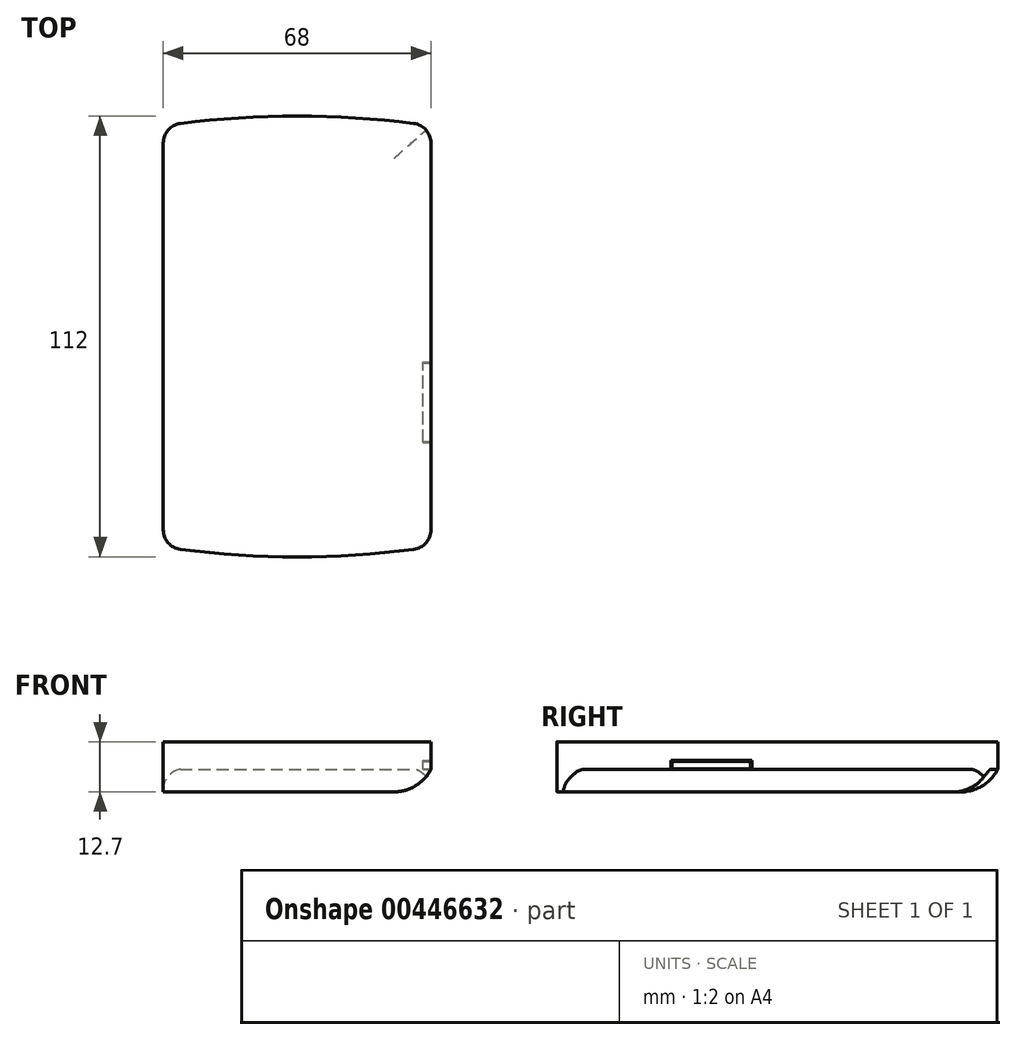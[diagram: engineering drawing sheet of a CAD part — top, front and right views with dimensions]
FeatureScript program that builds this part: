
annotation { "Feature Type Name" : "Feature", "Feature Type Description" : "" }
export const myFeature = defineFeature(function(context is Context, id is Id, definition is map)
    precondition{}
    {
        {
            var Q0;
            Q0=qCreatedBy(makeId("Top.planeOp"),FACE);
            var sketch = newSketch(context, id + "F0", { "sketchPlane" : qUnion([Q0])});
            skLineSegment(sketch, "E0.left", {"start": v(-34, 49.14) * mm, "end": v(-34, -49.14) * mm});
            skLineSegment(sketch, "E0.right", {"start": v(34, 49.14) * mm, "end": v(34, -49.14) * mm});
            skLineSegment(sketch, "E1", {"start": v(-34, 0) * mm, "end": v(34, 0) * mm, "construction": true});
            skArc(sketch, "E2", {"start": v(29.64, 54.1) * mm, "mid": v(0, 56) * mm, "end": v(-29.64, 54.1) * mm});
            skArc(sketch, "E3", {"start": v(-29.64, -54.1) * mm, "mid": v(0, -56) * mm, "end": v(29.64, -54.1) * mm});
            skLineSegment(sketch, "E4", {"start": v(0, 56) * mm, "end": v(0, -56) * mm, "construction": true});
            skPoint(sketch, "E5.visualSharp", {"position": v(-34, 53.5) * mm});
            skArc(sketch, "E5.filletArc", {"start": v(-29.64, 54.1) * mm, "mid": v(-32.75, 52.45) * mm, "end": v(-34, 49.14) * mm});
            skPoint(sketch, "E6.visualSharp", {"position": v(34, 53.5) * mm});
            skArc(sketch, "E6.filletArc", {"start": v(34, 49.14) * mm, "mid": v(32.75, 52.45) * mm, "end": v(29.64, 54.1) * mm});
            skPoint(sketch, "E7.visualSharp", {"position": v(34, -53.5) * mm});
            skArc(sketch, "E7.filletArc", {"start": v(29.64, -54.1) * mm, "mid": v(32.75, -52.45) * mm, "end": v(34, -49.14) * mm});
            skPoint(sketch, "E8.visualSharp", {"position": v(-34, -53.5) * mm});
            skArc(sketch, "E8.filletArc", {"start": v(-34, -49.14) * mm, "mid": v(-32.75, -52.45) * mm, "end": v(-29.64, -54.1) * mm});
            skLineSegment(sketch, "E9", {"start": v(-34, 49.14) * mm, "end": v(34, 49.14) * mm, "construction": true});
            skLineSegment(sketch, "E10", {"start": v(-34, -49.14) * mm, "end": v(34, -49.14) * mm, "construction": true});
            skSolve(sketch);
        }
        {
            var Q0;
            Q0=makeQuery(id+"F0.imprint","IMPRINT",FACE,{"disambiguationData":[TD([[makeQuery(id+"F0.imprint","IMPRINT",EDGE,{"derivedFrom":sQuery(id+"F0.wireOp",EDGE,"E0.left")}),1.0]])]});
            extrude(context, id + "F1", {"entities" : qUnion([Q0]), "oppositeDirection" : true, "depth" : 12.7 * mm});
        }
        {
            var Q0;
            Q0=qCreatedBy(makeId("Right.planeOp"),FACE);
            var sketch = newSketch(context, id + "F2", { "sketchPlane" : qUnion([Q0])});
            skLineSegment(sketch, "E11", {"start": v(56, 0) * mm, "end": v(56, -12.7) * mm, "construction": true});
            skLineSegment(sketch, "E12", {"start": v(56, 0) * mm, "end": v(66, 0) * mm});
            skLineSegment(sketch, "E13", {"start": v(66, 0) * mm, "end": v(66, -12.7) * mm});
            skLineSegment(sketch, "E14", {"start": v(66, -12.7) * mm, "end": v(46.6, -12.7) * mm});
            skLineSegment(sketch, "E15", {"start": v(56, 0) * mm, "end": v(56, -7) * mm});
            skLineSegment(sketch, "E16.0", {"start": v(49.14, -12.7) * mm, "end": v(-49.14, -12.7) * mm, "construction": true});
            skArc(sketch, "E17", {"start": v(46.6, -12.7) * mm, "mid": v(52.1, -11.16) * mm, "end": v(56, -7) * mm});
            skLineSegment(sketch, "E18", {"start": v(-176.45, 0) * mm, "end": v(-176.45, -17.3) * mm, "construction": true});
            skPoint(sketch, "E19.0", {"position": v(-176.45, 0) * mm});
            skLineSegment(sketch, "E20", {"start": v(0, 0) * mm, "end": v(0, -12.7) * mm, "construction": true});
            skLineSegment(sketch, "E21.MirrorCS", {"start": v(-56, 0) * mm, "end": v(-66, 0) * mm});
            skLineSegment(sketch, "E22.MirrorCS", {"start": v(-56, 0) * mm, "end": v(-56, -12.7) * mm, "construction": true});
            skArc(sketch, "E23.MirrorCS", {"start": v(-46.6, -12.7) * mm, "mid": v(-52.1, -11.16) * mm, "end": v(-56, -7) * mm});
            skLineSegment(sketch, "E24.MirrorCS", {"start": v(-66, -12.7) * mm, "end": v(-46.6, -12.7) * mm});
            skLineSegment(sketch, "E25.MirrorCS", {"start": v(-66, 0) * mm, "end": v(-66, -12.7) * mm});
            skLineSegment(sketch, "E26.MirrorCS", {"start": v(-56, 0) * mm, "end": v(-56, -7) * mm});
            skSolve(sketch);
        }
        {
            var Q0;
            Q0=makeQuery(id+"F2.imprint","IMPRINT",FACE,{"disambiguationData":[TD([[makeQuery(id+"F2.imprint","IMPRINT",EDGE,{"derivedFrom":sQuery(id+"F2.wireOp",EDGE,"E12")}),-1.0]])]});
            var Q1;
            Q1=sQuery(id+"F2.wireOp",EDGE,"E18");
            revolve(context, id + "F3", {"operationType" : NewBodyOperationType.REMOVE, "entities" : qUnion([Q0]), "axis" : qUnion([Q1]), "revolveType" : RevolveType.FULL, "oppositeDirection" : true});
        }
        {
            var Q0;
            Q0=qCreatedBy(makeId("Front.planeOp"),FACE);
            var sketch = newSketch(context, id + "F4", { "sketchPlane" : qUnion([Q0])});
            skFitSpline(sketch, "E27.0.2", {"points": [v(34, -12.7) * mm, v(34, -12.27) * mm, v(34, -11.83) * mm, v(34, -11.4) * mm], "construction": true});
            skLineSegment(sketch, "E27.0.3", {"start": v(34, -11.4) * mm, "end": v(34, 0) * mm, "construction": true});
            skLineSegment(sketch, "E27.0.5", {"start": v(34, 0) * mm, "end": v(34, -11.4) * mm, "construction": true});
            skLineSegment(sketch, "E28", {"start": v(34, 0) * mm, "end": v(44, 0) * mm});
            skLineSegment(sketch, "E29", {"start": v(44, 0) * mm, "end": v(44, -12.7) * mm});
            skLineSegment(sketch, "E30", {"start": v(44, -12.7) * mm, "end": v(24.6, -12.7) * mm});
            skLineSegment(sketch, "E31", {"start": v(34, 0) * mm, "end": v(34, -7) * mm});
            skArc(sketch, "E32", {"start": v(24.6, -12.7) * mm, "mid": v(30.1, -11.16) * mm, "end": v(34, -7) * mm});
            skSolve(sketch);
        }
        {
            var Q0;
            Q0=makeQuery(id+"F4.imprint","IMPRINT",FACE,{"disambiguationData":[TD([[makeQuery(id+"F4.imprint","IMPRINT",EDGE,{"derivedFrom":sQuery(id+"F4.wireOp",EDGE,"E28")}),-1.0]])]});
            extrude(context, id + "F5", {"entities" : qUnion([Q0]), "operationType" : NewBodyOperationType.REMOVE, "endBound" : BoundingType.SYMMETRIC, "depth" : 200 * mm});
        }
        {
            var Q0;
            Q0=makeQuery(id+"F1.opExtrude","SWEPT_FACE",FACE,{"disambiguationData":[OSD([sQuery(id+"F0.wireOp",EDGE,"E0.right")])]});
            var sketch = newSketch(context, id + "F6", { "sketchPlane" : qUnion([Q0])});
            skPoint(sketch, "E33.0", {"position": v(-56, 0) * mm});
            skLineSegment(sketch, "E34.bottom", {"start": v(-27, -7.2) * mm, "end": v(-6.5, -7.2) * mm});
            skLineSegment(sketch, "E34.top", {"start": v(-27, -4.7) * mm, "end": v(-6.5, -4.7) * mm});
            skLineSegment(sketch, "E34.left", {"start": v(-27, -7.2) * mm, "end": v(-27, -4.7) * mm});
            skLineSegment(sketch, "E34.right", {"start": v(-6.5, -7.2) * mm, "end": v(-6.5, -4.7) * mm});
            skLineSegment(sketch, "E35.0", {"start": v(-26.7, -5) * mm, "end": v(-6.8, -5) * mm});
            skLineSegment(sketch, "E35.1", {"start": v(-26.7, -6.9) * mm, "end": v(-26.7, -5) * mm});
            skLineSegment(sketch, "E35.2", {"start": v(-26.7, -6.9) * mm, "end": v(-6.8, -6.9) * mm});
            skLineSegment(sketch, "E35.3", {"start": v(-6.8, -6.9) * mm, "end": v(-6.8, -5) * mm});
            skSolve(sketch);
        }
        {
            var Q0;
            {var subQ1=sQuery(id+"F6.wireOp",EDGE,"E34.top");Q0=makeQuery(id+"F6.imprint","IMPRINT",FACE,{"disambiguationData":[TD([[makeQuery(id+"F6.imprint","IMPRINT",EDGE,{"derivedFrom":subQ1}),-1.0]])]});}
            extrude(context, id + "F7", {"entities" : qUnion([Q0]), "operationType" : NewBodyOperationType.REMOVE, "oppositeDirection" : true, "depth" : 2 * mm});
        }
    });
